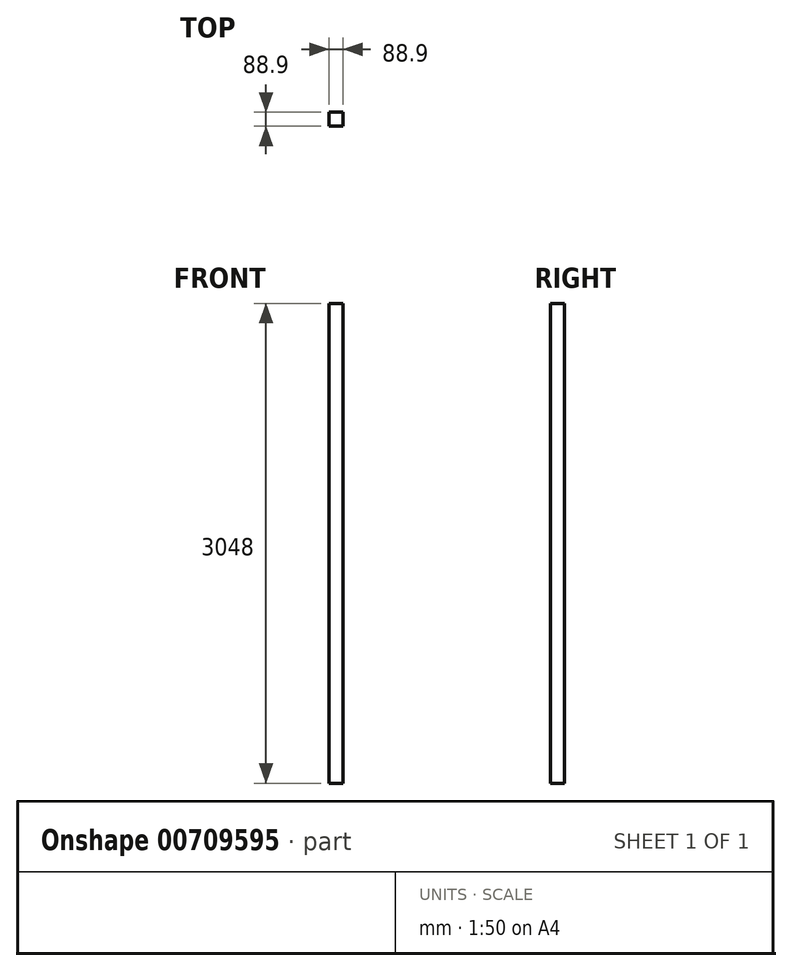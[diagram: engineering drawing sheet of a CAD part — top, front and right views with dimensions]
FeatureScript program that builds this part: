
annotation { "Feature Type Name" : "Feature", "Feature Type Description" : "" }
export const myFeature = defineFeature(function(context is Context, id is Id, definition is map)
    precondition{}
    {
        {
            var Q0;
            Q0=qCreatedBy(makeId("Top.planeOp"),FACE);
            var sketch = newSketch(context, id + "F0", { "sketchPlane" : qUnion([Q0])});
            skLineSegment(sketch, "E0.bottom", {"start": v(44.45, 44.45) * mm, "end": v(-44.45, 44.45) * mm});
            skLineSegment(sketch, "E0.top", {"start": v(44.45, -44.45) * mm, "end": v(-44.45, -44.45) * mm});
            skLineSegment(sketch, "E0.left", {"start": v(44.45, 44.45) * mm, "end": v(44.45, -44.45) * mm});
            skLineSegment(sketch, "E0.right", {"start": v(-44.45, 44.45) * mm, "end": v(-44.45, -44.45) * mm});
            skPoint(sketch, "E0.middle", {"position": v(0, 0) * mm});
            skSolve(sketch);
        }
        {
            var Q0;
            Q0=makeQuery(id+"F0.imprint","IMPRINT",FACE,{"disambiguationData":[TD([[makeQuery(id+"F0.imprint","IMPRINT",EDGE,{"derivedFrom":sQuery(id+"F0.wireOp",EDGE,"E0.bottom")}),1.0]])]});
            extrude(context, id + "F1", {"entities" : qUnion([Q0]), "depth" : 3048 * mm, "offsetDistance" : 25.4 * mm});
        }
    });
